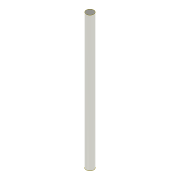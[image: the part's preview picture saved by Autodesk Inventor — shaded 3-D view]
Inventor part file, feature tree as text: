
AUTODESK INVENTOR PART (.ipt)
format: ipt  version: 2022 (Build 260153000, 153)  size: 74,752 bytes
history: native  units: mm
features: extrude x1, sketch x1
ambient origin geometry x8: Origin, YZ Plane, XZ Plane, XY Plane, X Axis, Y Axis, Z Axis, Center Point
bodies: Solid1 (feature_tree)
feature tree (2):
  extrude  "Extrusion1"  Depth=36.0mm TaperAngle=0.0deg
  sketch  "Sketch1"  dims[d0=2.0mm d1=36.0mm d2=0.0mm]
